# Revit family: НЕВАТОМ_Решетка защитная VR-KP AxB, Версия 1
name_source: partatom
category: Арматура воздуховодов
revit_build: Autodesk Revit 2017 (Build: 20170118_1100(x64)
units: mm (PartAtom-declared; Revit-internal decimal feet)

## family parameters
Всегда вертикально = Нет
На основе рабочей плоскости = Нет
Общий = Нет
При загрузке вырезать с полостями = Нет
Размер круглого соединителя = Использовать диаметр
Тип детали = Вставляется

## types (12) — shared parameters
ADSK_Единица измерения = шт.
ADSK_Завод-изготовитель = НЕВАТОМ
ADSK_Количество = 1
ADSK_Наименование = Защитная решетка для козырька
Nevatom_URL = https://t.me
т = 13 мм
толщина = 20 мм
шаг верт = 20 мм

## per-type parameters (varying)
| type | A ширина | A1 | ADSK_Марка | B длина | В1 |
| VR-KP 250-0,55/3000 | 142 мм | 380 мм | VR-KP-250-0,55/3000 | 390 мм | 132 мм |
| VR-KP 280-0,75/3000 | 169 мм | 380 мм | VR-KP-280-0,75/3000 | 390 мм | 159 мм |
| VR-KP 315-1,5/3000 | 196 мм | 480 мм | VR-KP 315-1,5/3000 | 490 мм | 186 мм |
| VR-KP 355-2,2/3000 | 221 мм | 480 мм | VR-KP-355-2,2/3000 | 490 мм | 211 мм |
| VR-KP 400-0,55/1500 | 235 мм | 630 мм | VR-KP-400-0,55/1500 | 640 мм | 225 мм |
| VR-KP 450-0,75/1500 | 258 мм | 630 мм | VR-KP-450-0,75/1500 | 640 мм | 248 мм |
| VR-KP 500-0,37/1000 | 287 мм | 780 мм | VR-KP-500-0,37/1000 | 790 мм | 277 мм |
| VR-KP 560-1,1/1000 | 334 мм | 780 мм | VR-KP-560-1,1/1000 | 790 мм | 324 мм |
| VR-KP 560-3/1500 | 344 мм | 780 мм | VR-KP-560-3/1500 | 790 мм | 334 мм |
| VR-KP 630-1,5/1000 | 370 мм | 980 мм | VR-KP-630-1,5/1000 | 990 мм | 360 мм |
| VR-KP 630-5,5/1500 | 400 мм | 980 мм | VR-KP-630-5,5/1500 | 990 мм | 390 мм |
| VR-KP 710-3/1000 | 439 мм | 980 мм | VR-KP-710-3/1000 | 990 мм | 429 мм |
